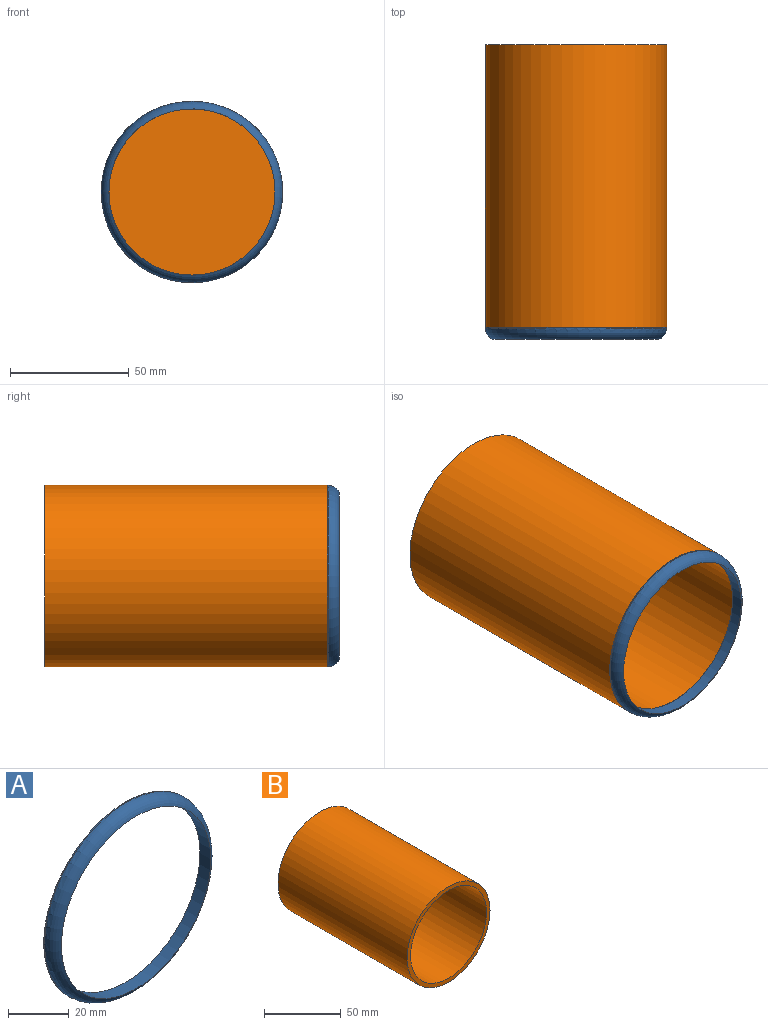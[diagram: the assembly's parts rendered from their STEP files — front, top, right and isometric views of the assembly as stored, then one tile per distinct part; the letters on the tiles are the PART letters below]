
ASSEMBLY  parts=2 mates=1
PART A: 4 faces, bbox 82.5x5.5x82.5 mm
  f0: cylinder r=34.92mm len=69.85mm, axis (0,1,0), area 1114.8mm2, adj f2,f3
  f1: cylinder r=38.1mm len=76.2mm, axis (0,1,0), area 88.7mm2, adj f2,f3
  f2: plane 76.2x76.2mm, normal (0,1,0), area 728.4mm2, adj f0,f1
  f3: torus R=33.02mm, axis (0,-1,0), area 1400.7mm2, adj f0,f1
PART B: 5 faces, bbox 76.2x118.7x76.2 mm
  f0: cylinder r=34.92mm len=109.22mm, axis (0,1,0), area 23967.3mm2, adj f2,f4
  f1: cylinder r=38.1mm len=118.75mm, axis (0,1,0), area 28426.3mm2, adj f2,f3
  f2: plane 76.2x76.2mm, normal (0,-1,0), area 728.4mm2, adj f0,f1
  f3: plane 76.2x76.2mm, normal (0,1,0), area 4560.4mm2, adj f1
  f4: plane 69.85x69.85mm, normal (0,-1,0), area 3832mm2, adj f0
PLACE A rot(axis=(0,1,0),180deg) t=(-23.88,-105.4,14.5)mm
PLACE B t=(-23.88,13.34,14.5)mm
MATE fastened A.f0 <-> B.f0  axis (0,-1,0) through (-23.88,-110.48,14.5)mm
